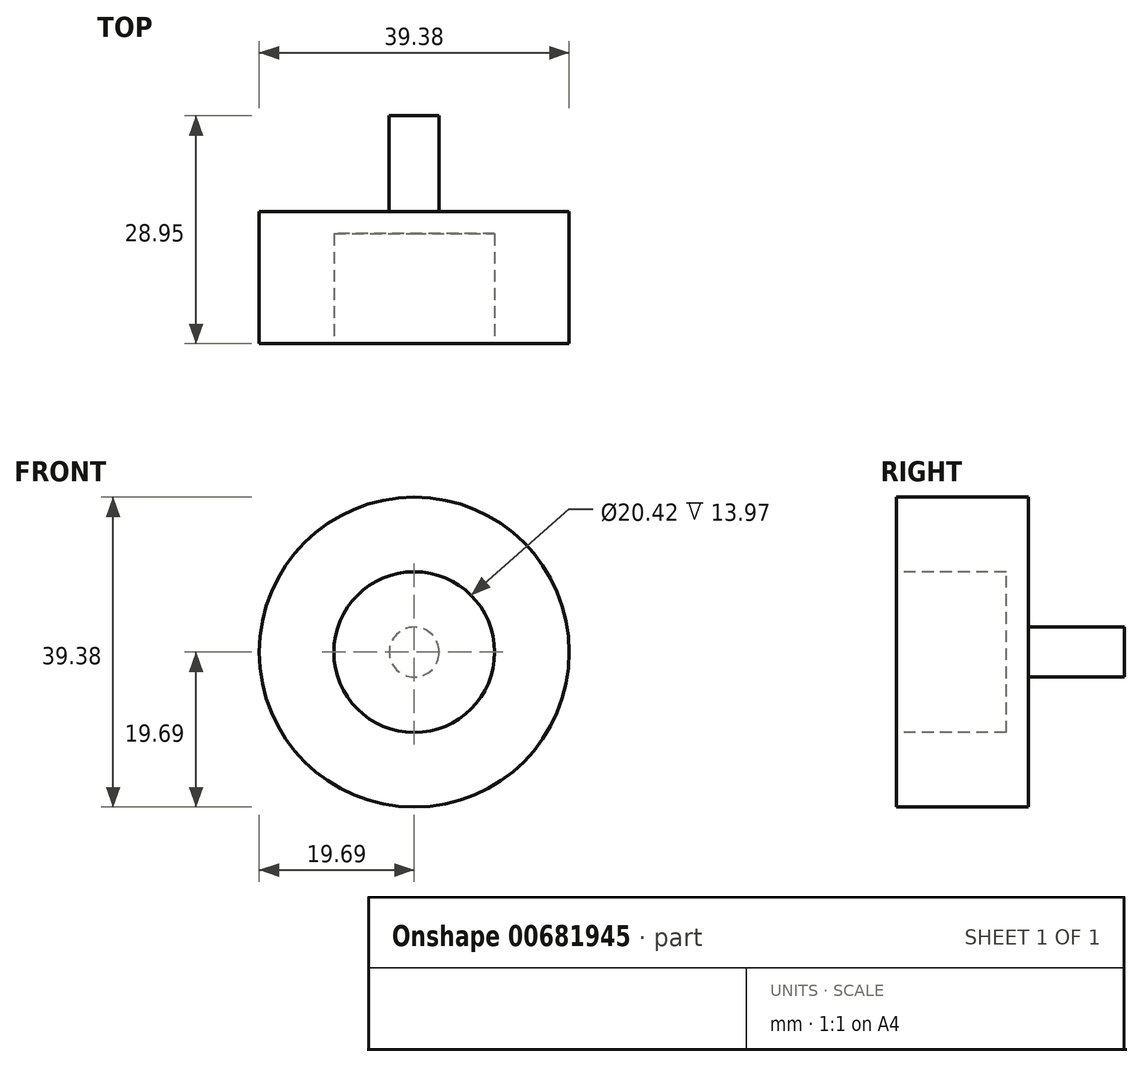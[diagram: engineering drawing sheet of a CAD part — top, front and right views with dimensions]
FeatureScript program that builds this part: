
annotation { "Feature Type Name" : "Feature", "Feature Type Description" : "" }
export const myFeature = defineFeature(function(context is Context, id is Id, definition is map)
    precondition{}
    {
        {
            var Q0;
            Q0=qCreatedBy(makeId("Front.planeOp"),FACE);
            var sketch = newSketch(context, id + "F0", { "sketchPlane" : qUnion([Q0])});
            skCircle(sketch, "E0", {"center": v(0, 0) * mm, "radius": 19.69 * mm});
            skSolve(sketch);
        }
        {
            var Q0;
            Q0 = qSketchRegion(id + "F0", true);
            extrude(context, id + "F1", {"entities" : qUnion([Q0]), "depth" : 16.76 * mm, "offsetDistance" : 25.4 * mm});
        }
        {
            var Q0;
            Q0=makeQuery(id+"F1.opExtrude","CAP_FACE",FACE,{"disambiguationData":[OSD([sQuery(id+"F0.wireOp",EDGE,"E0")])],"isStart":false});
            var sketch = newSketch(context, id + "F2", { "sketchPlane" : qUnion([Q0])});
            skCircle(sketch, "E1", {"center": v(0, 0) * mm, "radius": 10.21 * mm});
            skSolve(sketch);
        }
        {
            var Q0;
            Q0=makeQuery(id+"F2.imprint","IMPRINT",FACE,{"disambiguationData":[TD([[makeQuery(id+"F2.imprint","IMPRINT",EDGE,{"derivedFrom":sQuery(id+"F2.wireOp",EDGE,"E1")}),1.0]])]});
            extrude(context, id + "F3", {"entities" : qUnion([Q0]), "operationType" : NewBodyOperationType.REMOVE, "oppositeDirection" : true, "depth" : 13.97 * mm, "offsetDistance" : 25.4 * mm});
        }
        {
            var Q0;
            Q0=makeQuery(id+"F1.opExtrude","CAP_FACE",FACE,{"disambiguationData":[OSD([sQuery(id+"F0.wireOp",EDGE,"E0")])],"isStart":true});
            var sketch = newSketch(context, id + "F4", { "sketchPlane" : qUnion([Q0])});
            skCircle(sketch, "E2", {"center": v(0, 0) * mm, "radius": 3.18 * mm});
            skSolve(sketch);
        }
        {
            var Q0;
            Q0 = qSketchRegion(id + "F4", true);
            extrude(context, id + "F5", {"entities" : qUnion([Q0]), "operationType" : NewBodyOperationType.ADD, "depth" : 12.2 * mm, "offsetDistance" : 25.4 * mm});
        }
    });
